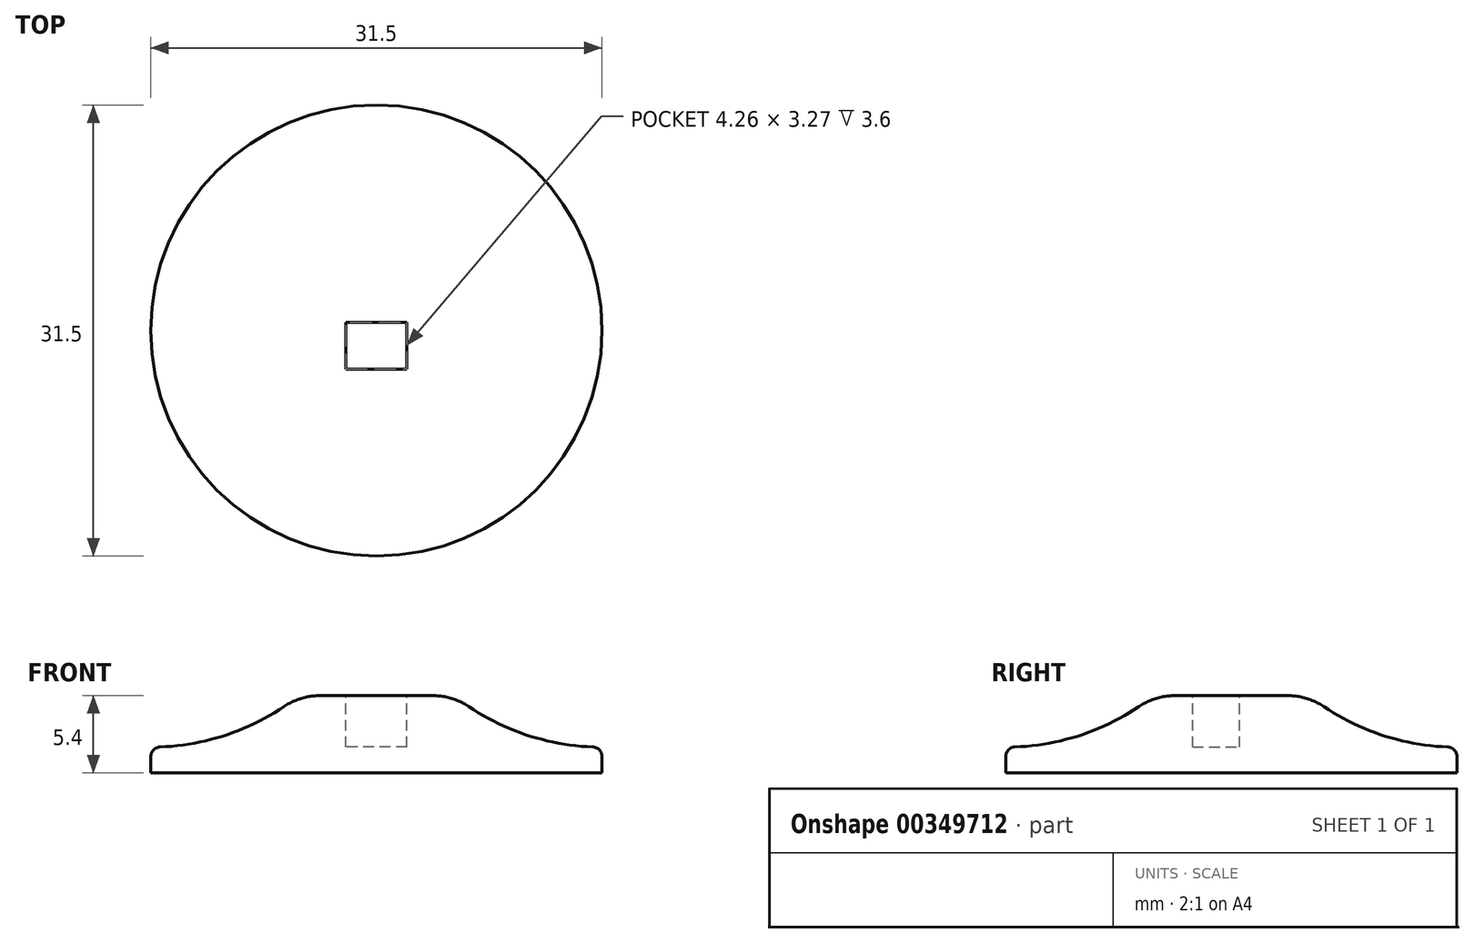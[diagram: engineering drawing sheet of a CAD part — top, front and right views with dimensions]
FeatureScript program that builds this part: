
annotation { "Feature Type Name" : "Feature", "Feature Type Description" : "" }
export const myFeature = defineFeature(function(context is Context, id is Id, definition is map)
    precondition{}
    {
        {
            var Q0;
            Q0=qCreatedBy(makeId("Right.planeOp"),FACE);
            var sketch = newSketch(context, id + "F0", { "sketchPlane" : qUnion([Q0])});
            skLineSegment(sketch, "E0.bottom", {"start": v(17.5, -1) * mm, "end": v(-17.5, -1) * mm});
            skLineSegment(sketch, "E0.top", {"start": v(17.5, 1) * mm, "end": v(-17.5, 1) * mm});
            skLineSegment(sketch, "E0.left", {"start": v(17.5, -1) * mm, "end": v(17.5, 1) * mm});
            skLineSegment(sketch, "E0.right", {"start": v(-17.5, -1) * mm, "end": v(-17.5, 1) * mm});
            skPoint(sketch, "E0.middle", {"position": v(0, 0) * mm});
            skLineSegment(sketch, "E1", {"start": v(0, 1) * mm, "end": v(0, 5) * mm});
            skLineSegment(sketch, "E2", {"start": v(-4.38, 5) * mm, "end": v(4.38, 5) * mm});
            skArc(sketch, "E3", {"start": v(-17.5, 1) * mm, "mid": v(-12.1, 1.8) * mm, "end": v(-7.16, 4.15) * mm});
            skArc(sketch, "E4", {"start": v(7.16, 4.15) * mm, "mid": v(12.1, 1.8) * mm, "end": v(17.5, 1) * mm});
            skPoint(sketch, "E5.visualSharp", {"position": v(-6, 5) * mm});
            skArc(sketch, "E5.filletArc", {"start": v(-4.38, 5) * mm, "mid": v(-5.83, 4.78) * mm, "end": v(-7.16, 4.15) * mm});
            skPoint(sketch, "E6.visualSharp", {"position": v(6, 5) * mm});
            skArc(sketch, "E6.filletArc", {"start": v(7.16, 4.15) * mm, "mid": v(5.83, 4.78) * mm, "end": v(4.38, 5) * mm});
            skLineSegment(sketch, "E7", {"start": v(0, 1) * mm, "end": v(0, -1) * mm});
            skLineSegment(sketch, "E8", {"start": v(0, -1) * mm, "end": v(0, 5) * mm});
            skSolve(sketch);
        }
        {
            var Q0;
            {var subQ1=sQuery(id+"F0.wireOp",EDGE,"E4");Q0=makeQuery(id+"F0.imprint","IMPRINT",FACE,{"disambiguationData":[TD([[makeQuery(id+"F0.imprint","IMPRINT",EDGE,{"derivedFrom":subQ1}),-1.0]])]});}
            var Q1;
            {var subQ0=sQuery(id+"F0.wireOp",EDGE,"E0.left");Q1=makeQuery(id+"F0.imprint","IMPRINT",FACE,{"disambiguationData":[TD([[makeQuery(id+"F0.imprint","IMPRINT",EDGE,{"derivedFrom":subQ0}),1.0]])]});}
            var Q2;
            Q2=sQuery(id+"F0.wireOp",EDGE,"E8");
            revolve(context, id + "F1", {"entities" : qUnion([Q0, Q1]), "axis" : qUnion([Q2]), "revolveType" : RevolveType.ONE_DIRECTION, "angle" : 360 * degree});
        }
        {
            var Q0;
            Q0=makeQuery(id+"F1.opRevolve","SWEPT_FACE",FACE,{"disambiguationData":[OSD([sQuery(id+"F0.wireOp",EDGE,"E2")])]});
            var sketch = newSketch(context, id + "F2", { "sketchPlane" : qUnion([Q0])});
            skLineSegment(sketch, "E9", {"start": v(0, 0) * mm, "end": v(0, -1) * mm});
            skLineSegment(sketch, "E10.bottom", {"start": v(2, -3) * mm, "end": v(-2, -3) * mm});
            skLineSegment(sketch, "E10.top", {"start": v(2, 1) * mm, "end": v(-2, 1) * mm});
            skLineSegment(sketch, "E10.left", {"start": v(2, -3) * mm, "end": v(2, 1) * mm});
            skLineSegment(sketch, "E10.right", {"start": v(-2, -3) * mm, "end": v(-2, 1) * mm});
            skPoint(sketch, "E10.middle", {"position": v(0, -1) * mm});
            skSolve(sketch);
        }
        {
            var Q0;
            Q0=makeQuery(id+"F2.imprint","IMPRINT",FACE,{"disambiguationData":[TD([[makeQuery(id+"F2.imprint","IMPRINT",EDGE,{"derivedFrom":sQuery(id+"F2.wireOp",EDGE,"E10.bottom")}),-1.0]])]});
            extrude(context, id + "F3", {"entities" : qUnion([Q0]), "operationType" : NewBodyOperationType.REMOVE, "oppositeDirection" : true, "depth" : 4 * mm});
        }
        {
            var Q0;
            Q0=makeQuery(id+"F1.opRevolve","SWEPT_EDGE",EDGE,{"disambiguationData":[OSD([sQuery(id+"F0.wireOp",EDGE,"E0.top"),sQuery(id+"F0.wireOp",EDGE,"E0.left"),sQuery(id+"F0.wireOp",EDGE,"E4")])]});
            fillet(context, id + "F4", {"entities" : qUnion([Q0]), "radius" : .75 * mm, "tangentPropagation" : true, "allowEdgeOverflow" : false});
        }
        {
            var Q0;
            Q0=makeQuery(id+"F1.opRevolve","SWEPT_BODY",BODY,{"disambiguationData":[OSD([sQuery(id+"F0.wireOp",EDGE,"E0.bottom"),sQuery(id+"F0.wireOp",EDGE,"E0.left"),sQuery(id+"F0.wireOp",EDGE,"E2"),sQuery(id+"F0.wireOp",EDGE,"E4"),sQuery(id+"F0.wireOp",EDGE,"E6.filletArc"),sQuery(id+"F0.wireOp",EDGE,"E8")])]});
            var Q1;
            Q1=qCreatedBy(makeId("Origin.pointOp"),VERTEX);
            transform(context, id + "F5", {"entities" : qUnion([Q0]), "transformType" : TransformType.SCALE_UNIFORMLY, "scale" : .9, "scalePoint" : qUnion([Q1]), "makeCopy" : false});
        }
        {
            var Q0;
            Q0=makeQuery(id+"F3.boolean.opBoolean","COPY",FACE,{"derivedFrom":makeQuery(id+"F3.opExtrude","SWEPT_FACE",FACE,{"disambiguationData":[OSD([sQuery(id+"F2.wireOp",EDGE,"E10.right")])]})});
            extrude(context, id + "F6", {"entities" : qUnion([Q0]), "operationType" : NewBodyOperationType.REMOVE, "oppositeDirection" : true, "depth" : .33 * mm});
        }
        {
            var Q0;
            Q0=makeQuery(id+"F3.boolean.opBoolean","COPY",FACE,{"derivedFrom":makeQuery(id+"F3.opExtrude","SWEPT_FACE",FACE,{"disambiguationData":[OSD([sQuery(id+"F2.wireOp",EDGE,"E10.left")])]})});
            extrude(context, id + "F7", {"entities" : qUnion([Q0]), "operationType" : NewBodyOperationType.REMOVE, "oppositeDirection" : true, "depth" : .33 * mm});
        }
        {
            var Q0;
            {var subQ0=sQuery(id+"F2.wireOp",EDGE,"E10.top");Q0=makeQuery(id+"F7.boolean.opBoolean","MERGE",FACE,{"derivedFrom":[makeQuery(id+"F6.boolean.opBoolean","MERGE",FACE,{"derivedFrom":[makeQuery(id+"F3.boolean.opBoolean","COPY",FACE,{"derivedFrom":makeQuery(id+"F3.opExtrude","SWEPT_FACE",FACE,{"disambiguationData":[OSD([subQ0])]})}),makeQuery(id+"F6.opExtrude","SWEPT_FACE",FACE,{"disambiguationData":[OSD([subQ0,sQuery(id+"F2.wireOp",EDGE,"E10.right")])]})]}),makeQuery(id+"F7.opExtrude","SWEPT_FACE",FACE,{"disambiguationData":[OSD([subQ0,sQuery(id+"F2.wireOp",EDGE,"E10.left")])]})]});}
            extrude(context, id + "F8", {"entities" : qUnion([Q0]), "operationType" : NewBodyOperationType.ADD, "depth" : .33 * mm});
        }
    });
